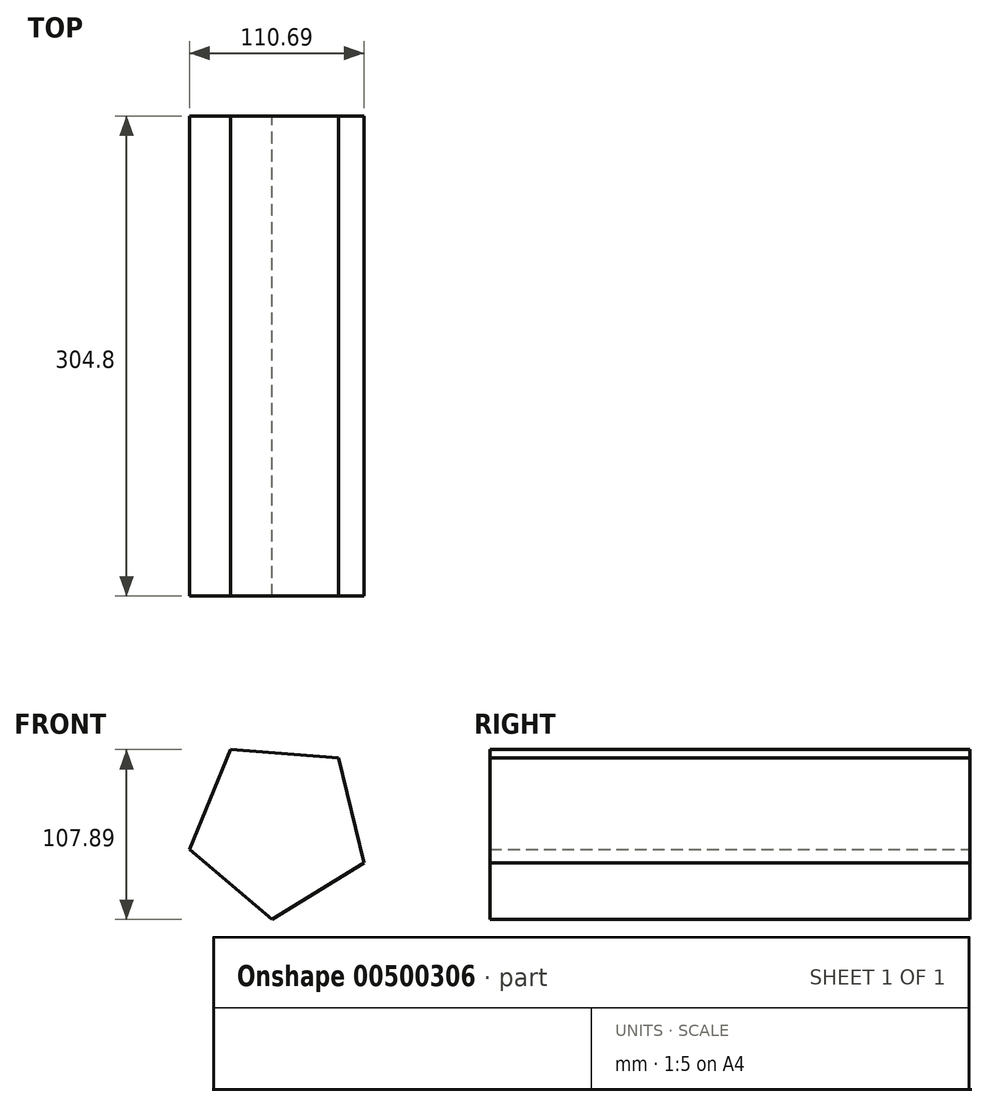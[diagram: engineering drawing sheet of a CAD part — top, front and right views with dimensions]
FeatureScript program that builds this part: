
annotation { "Feature Type Name" : "Feature", "Feature Type Description" : "" }
export const myFeature = defineFeature(function(context is Context, id is Id, definition is map)
    precondition{}
    {
        {
            var Q0;
            Q0=qCreatedBy(makeId("Front.planeOp"),FACE);
            var sketch = newSketch(context, id + "F0", { "sketchPlane" : qUnion([Q0])});
            skCircle(sketch, "E0.cCircle", {"center": v(0, 0) * mm, "radius": 58.36 * mm, "construction": true});
            skLineSegment(sketch, "E0.0", {"start": v(-30.6, 49.7) * mm, "end": v(37.8, 44.46) * mm});
            skLineSegment(sketch, "E0.1", {"start": v(37.8, 44.46) * mm, "end": v(53.97, -22.22) * mm});
            skLineSegment(sketch, "E0.2", {"start": v(53.97, -22.22) * mm, "end": v(-4.45, -58.2) * mm});
            skLineSegment(sketch, "E0.3", {"start": v(-4.45, -58.2) * mm, "end": v(-56.72, -13.75) * mm});
            skLineSegment(sketch, "E0.4", {"start": v(-56.72, -13.75) * mm, "end": v(-30.6, 49.7) * mm});
            skSolve(sketch);
        }
        {
            var Q0;
            Q0=makeQuery(id+"F0.imprint","IMPRINT",FACE,{"disambiguationData":[TD([[makeQuery(id+"F0.imprint","IMPRINT",EDGE,{"derivedFrom":sQuery(id+"F0.wireOp",EDGE,"E0.0")}),-1.0]])]});
            extrude(context, id + "F1", {"entities" : qUnion([Q0]), "depth" : 304.8 * mm});
        }
    });
